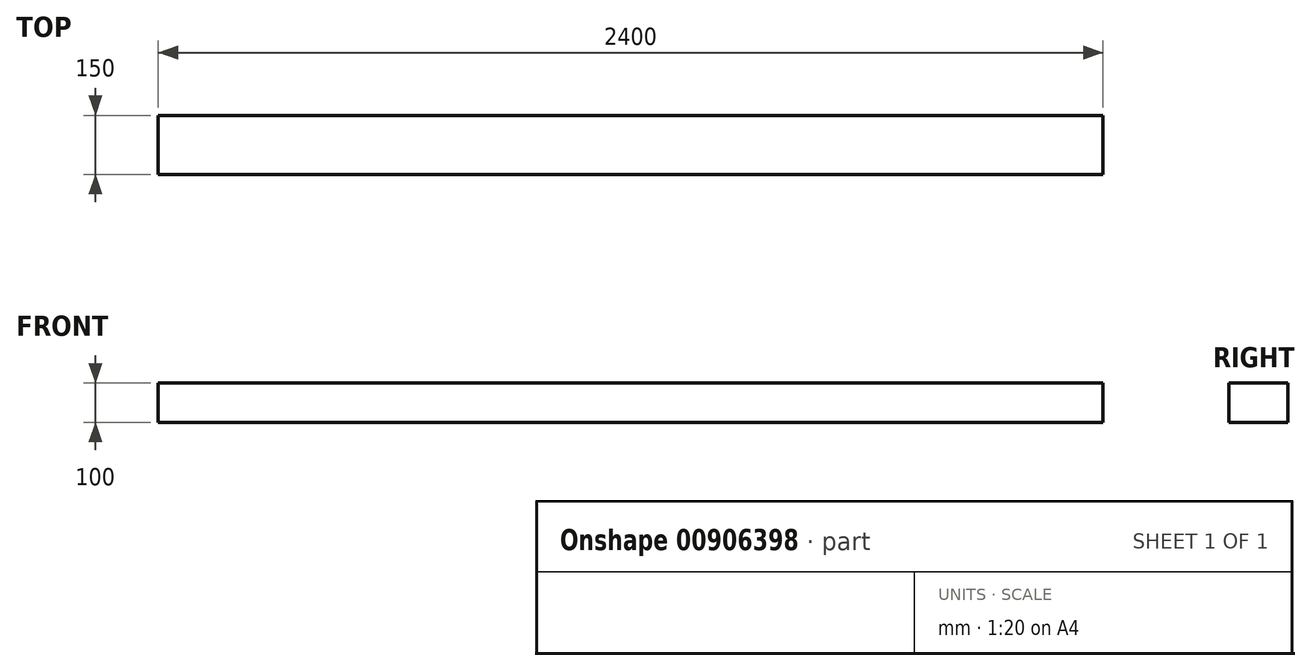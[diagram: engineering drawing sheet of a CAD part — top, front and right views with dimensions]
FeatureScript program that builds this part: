
annotation { "Feature Type Name" : "Feature", "Feature Type Description" : "" }
export const myFeature = defineFeature(function(context is Context, id is Id, definition is map)
    precondition{}
    {
        {
            var Q0;
            Q0=qCreatedBy(makeId("Right.planeOp"),FACE);
            var sketch = newSketch(context, id + "F0", { "sketchPlane" : qUnion([Q0])});
            skLineSegment(sketch, "E0.bottom", {"start": v(0, 0) * mm, "end": v(150, 0) * mm});
            skLineSegment(sketch, "E0.top", {"start": v(0, 100) * mm, "end": v(150, 100) * mm});
            skLineSegment(sketch, "E0.left", {"start": v(0, 0) * mm, "end": v(0, 100) * mm});
            skLineSegment(sketch, "E0.right", {"start": v(150, 0) * mm, "end": v(150, 100) * mm});
            skSolve(sketch);
        }
        {
            var Q0;
            Q0 = qSketchRegion(id + "F0", true);
            extrude(context, id + "F1", {"entities" : qUnion([Q0]), "depth" : 2400 * mm, "offsetDistance" : 25 * mm});
        }
    });
